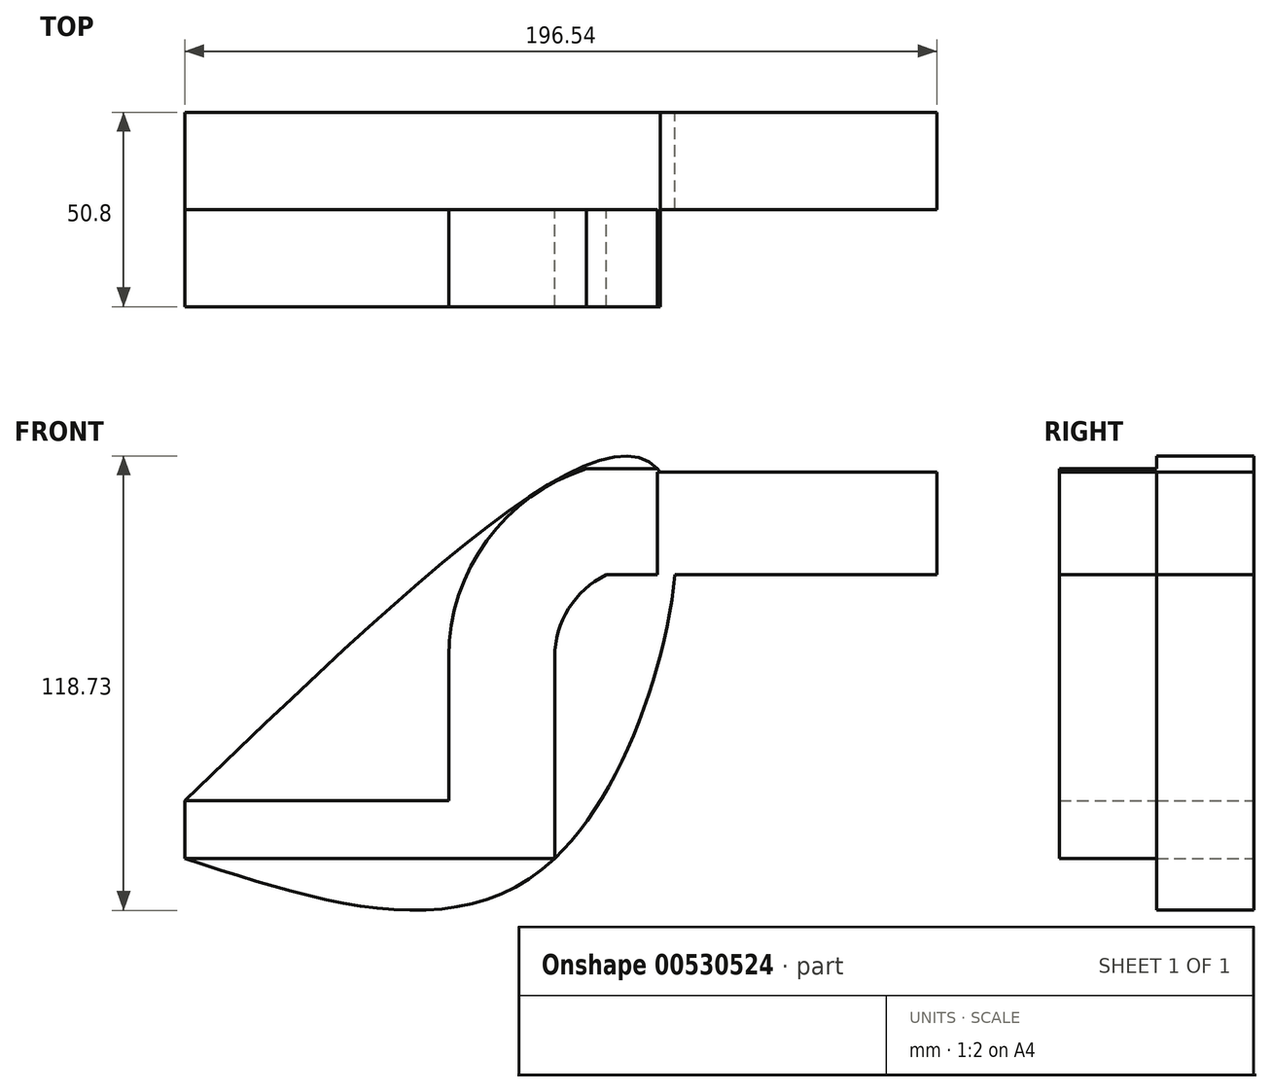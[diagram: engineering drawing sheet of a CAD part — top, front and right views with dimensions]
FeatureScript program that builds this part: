
annotation { "Feature Type Name" : "Feature", "Feature Type Description" : "" }
export const myFeature = defineFeature(function(context is Context, id is Id, definition is map)
    precondition{}
    {
        {
            var Q0;
            Q0=qCreatedBy(makeId("Front.planeOp"),FACE);
            var sketch = newSketch(context, id + "F0", { "sketchPlane" : qUnion([Q0])});
            skLineSegment(sketch, "E0.bottom", {"start": v(-48.33, 7.52) * mm, "end": v(48.33, 7.52) * mm});
            skLineSegment(sketch, "E0.top", {"start": v(-48.33, -7.52) * mm, "end": v(48.33, -7.52) * mm});
            skLineSegment(sketch, "E0.left", {"start": v(-48.33, 7.52) * mm, "end": v(-48.33, -7.52) * mm});
            skLineSegment(sketch, "E0.right", {"start": v(48.33, 7.52) * mm, "end": v(48.33, -7.52) * mm});
            skPoint(sketch, "E0.middle", {"position": v(0, 0) * mm});
            skLineSegment(sketch, "E1.bottom", {"start": v(75.18, 93.43) * mm, "end": v(148.2, 93.43) * mm});
            skLineSegment(sketch, "E1.top", {"start": v(75.18, 66.59) * mm, "end": v(148.2, 66.59) * mm});
            skLineSegment(sketch, "E1.left", {"start": v(75.18, 93.43) * mm, "end": v(75.18, 66.59) * mm});
            skLineSegment(sketch, "E1.right", {"start": v(148.2, 93.43) * mm, "end": v(148.2, 66.59) * mm});
            skPoint(sketch, "E1.middle", {"position": v(111.7, 80.01) * mm});
            skLineSegment(sketch, "E2", {"start": v(48.33, 7.52) * mm, "end": v(48.33, 45.1) * mm});
            skLineSegment(sketch, "E3", {"start": v(75.18, 66.59) * mm, "end": v(61.75, 66.59) * mm});
            skArc(sketch, "E4", {"start": v(48.33, 45.1) * mm, "mid": v(51.96, 57.77) * mm, "end": v(61.75, 66.59) * mm});
            skLineSegment(sketch, "E5.0", {"start": v(75.18, 94.27) * mm, "end": v(56.62, 94.27) * mm});
            skArc(sketch, "E5.1", {"start": v(20.64, 45.1) * mm, "mid": v(30.6, 75.57) * mm, "end": v(56.62, 94.27) * mm});
            skLineSegment(sketch, "E5.2", {"start": v(20.64, 7.52) * mm, "end": v(20.64, 45.1) * mm});
            skFitSpline(sketch, "E6", {"points": [v(-48.33, 7.52) * mm, v(75.18, 94.27) * mm, v(48.33, -7.52) * mm, v(-48.33, -7.52) * mm], "startDerivative": vector(426.9, 411.4) * mm, "endDerivative": vector(-354.74, 115.93) * mm});
            skSolve(sketch);
        }
        {
            var Q0;
            Q0=makeQuery(id+"F0.imprint","IMPRINT",FACE,{"disambiguationData":[TD([[makeQuery(id+"F0.imprint","IMPRINT",EDGE,{"derivedFrom":sQuery(id+"F0.wireOp",EDGE,"E0.top")}),1.0]])]});
            var Q1;
            {var subQ0=sQuery(id+"F0.wireOp",EDGE,"E1.left");Q1=makeQuery(id+"F0.imprint","IMPRINT",FACE,{"disambiguationData":[TD([[makeQuery(id+"F0.imprint","IMPRINT",EDGE,{"derivedFrom":subQ0}),-1.0]])]});}
            extrude(context, id + "F1", {"entities" : qUnion([Q0, Q1]), "depth" : 50.8 * mm, "offsetDistance" : 25.4 * mm});
        }
        {
            var Q0;
            Q0 = qSketchRegion(id + "F0", true);
            extrude(context, id + "F2", {"entities" : qUnion([Q0]), "operationType" : NewBodyOperationType.ADD, "depth" : 25.4 * mm, "offsetDistance" : 25.4 * mm});
        }
    });
